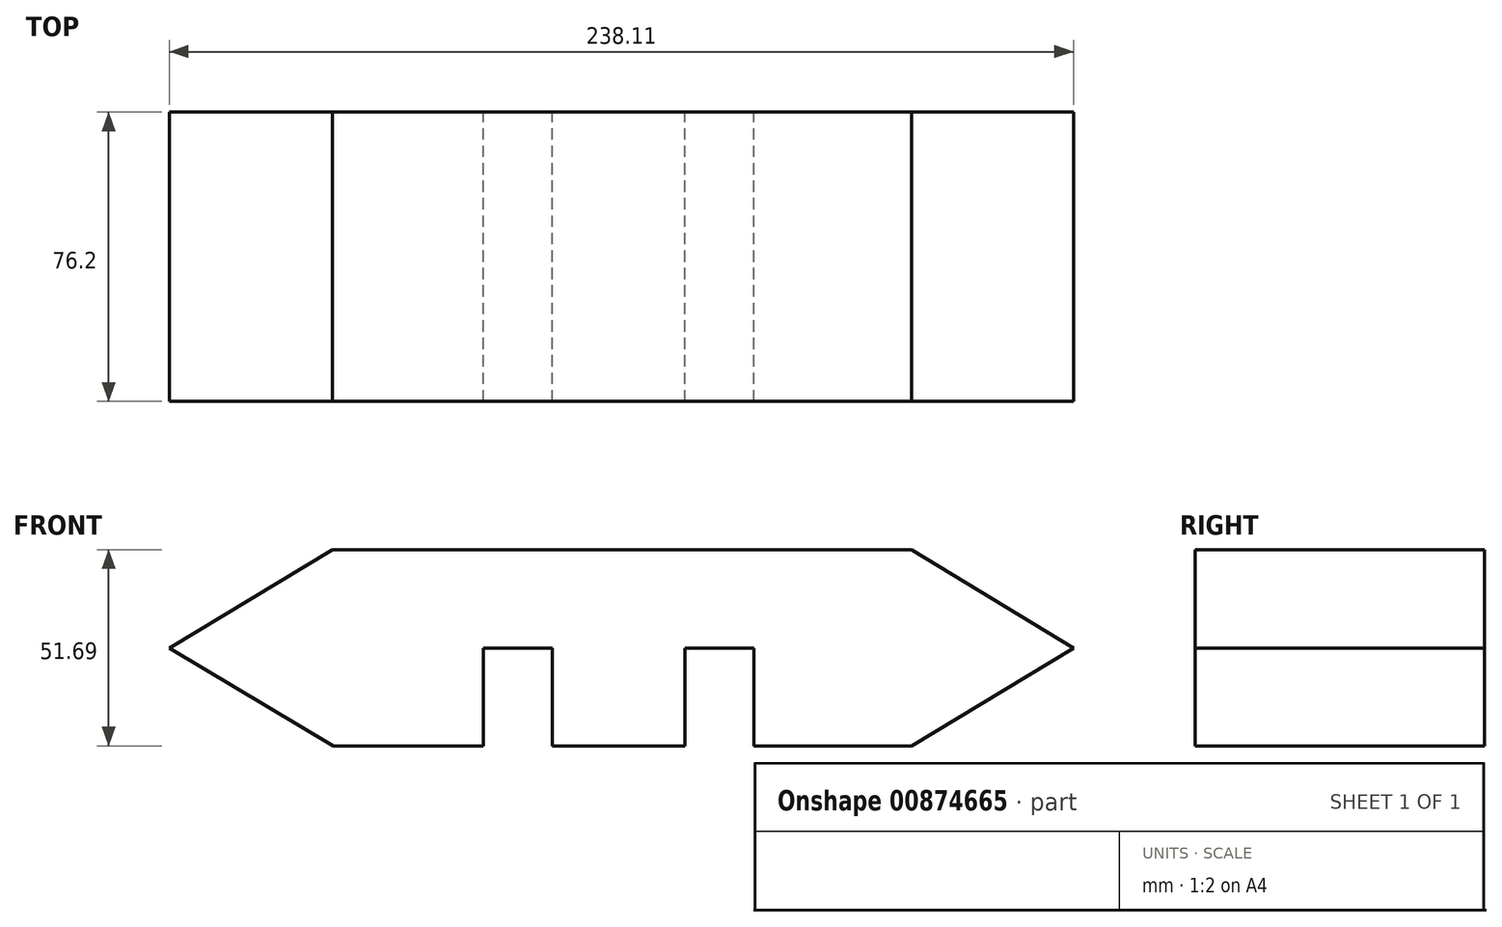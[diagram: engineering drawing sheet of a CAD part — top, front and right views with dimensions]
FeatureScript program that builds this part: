
annotation { "Feature Type Name" : "Feature", "Feature Type Description" : "" }
export const myFeature = defineFeature(function(context is Context, id is Id, definition is map)
    precondition{}
    {
        {
            var Q0;
            Q0=qCreatedBy(makeId("Front.planeOp"),FACE);
            var sketch = newSketch(context, id + "F0", { "sketchPlane" : qUnion([Q0])});
            skLineSegment(sketch, "E0", {"start": v(-76.2, 25.98) * mm, "end": v(-119.09, 0) * mm});
            skLineSegment(sketch, "E1", {"start": v(-119.09, 0) * mm, "end": v(-75.92, -25.71) * mm});
            skLineSegment(sketch, "E2", {"start": v(-75.92, -25.71) * mm, "end": v(-36.33, -25.71) * mm});
            skLineSegment(sketch, "E3", {"start": v(-36.33, -25.71) * mm, "end": v(-36.33, 0) * mm});
            skLineSegment(sketch, "E4", {"start": v(-36.33, 0) * mm, "end": v(-18.18, 0) * mm});
            skLineSegment(sketch, "E5", {"start": v(-18.18, 0) * mm, "end": v(-18.18, -25.71) * mm});
            skLineSegment(sketch, "E6", {"start": v(-18.18, -25.71) * mm, "end": v(16.74, -25.71) * mm});
            skLineSegment(sketch, "E7", {"start": v(16.74, -25.71) * mm, "end": v(16.74, 0) * mm});
            skLineSegment(sketch, "E8", {"start": v(16.74, 0) * mm, "end": v(34.88, 0) * mm});
            skLineSegment(sketch, "E9", {"start": v(34.88, 0) * mm, "end": v(34.88, -25.71) * mm});
            skLineSegment(sketch, "E10", {"start": v(34.88, -25.71) * mm, "end": v(76.4, -25.71) * mm});
            skLineSegment(sketch, "E11", {"start": v(76.4, -25.71) * mm, "end": v(119.02, 0) * mm});
            skLineSegment(sketch, "E12", {"start": v(119.02, 0) * mm, "end": v(76.4, 25.98) * mm});
            skLineSegment(sketch, "E13", {"start": v(76.4, 25.98) * mm, "end": v(-76.2, 25.98) * mm});
            skSolve(sketch);
        }
        {
            var Q0;
            Q0=makeQuery(id+"F0.imprint","IMPRINT",FACE,{"disambiguationData":[TD([[makeQuery(id+"F0.imprint","IMPRINT",EDGE,{"derivedFrom":sQuery(id+"F0.wireOp",EDGE,"E0")}),1.0]])]});
            extrude(context, id + "F1", {"entities" : qUnion([Q0]), "depth" : 76.2 * mm, "offsetDistance" : 25.4 * mm});
        }
    });
